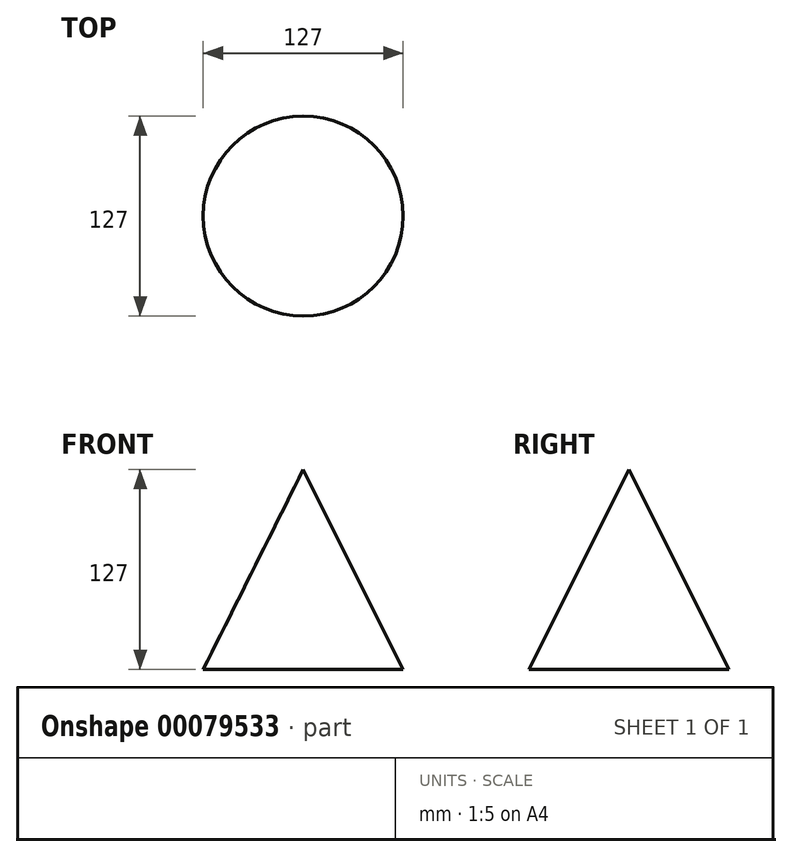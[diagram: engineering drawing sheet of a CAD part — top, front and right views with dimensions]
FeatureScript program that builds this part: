
annotation { "Feature Type Name" : "Feature", "Feature Type Description" : "" }
export const myFeature = defineFeature(function(context is Context, id is Id, definition is map)
    precondition{}
    {
        {
            var Q0;
            Q0=qCreatedBy(makeId("Front.planeOp"),FACE);
            var sketch = newSketch(context, id + "F0", { "sketchPlane" : qUnion([Q0])});
            skLineSegment(sketch, "E0", {"start": v(0, 0) * mm, "end": v(0, 127) * mm});
            skLineSegment(sketch, "E1", {"start": v(0, 0) * mm, "end": v(-63.5, 0) * mm});
            skLineSegment(sketch, "E2", {"start": v(-63.5, 0) * mm, "end": v(0, 127) * mm});
            skPoint(sketch, "E3.orphan", {"position": v(63.5, 0) * mm});
            skSolve(sketch);
        }
        {
            var Q0;
            Q0 = qSketchRegion(id + "F0", true);
            var Q1;
            Q1=sQuery(id+"F0.wireOp",EDGE,"E0");
            revolve(context, id + "F1", {"entities" : qUnion([Q0]), "axis" : qUnion([Q1]), "revolveType" : RevolveType.FULL});
        }
    });
